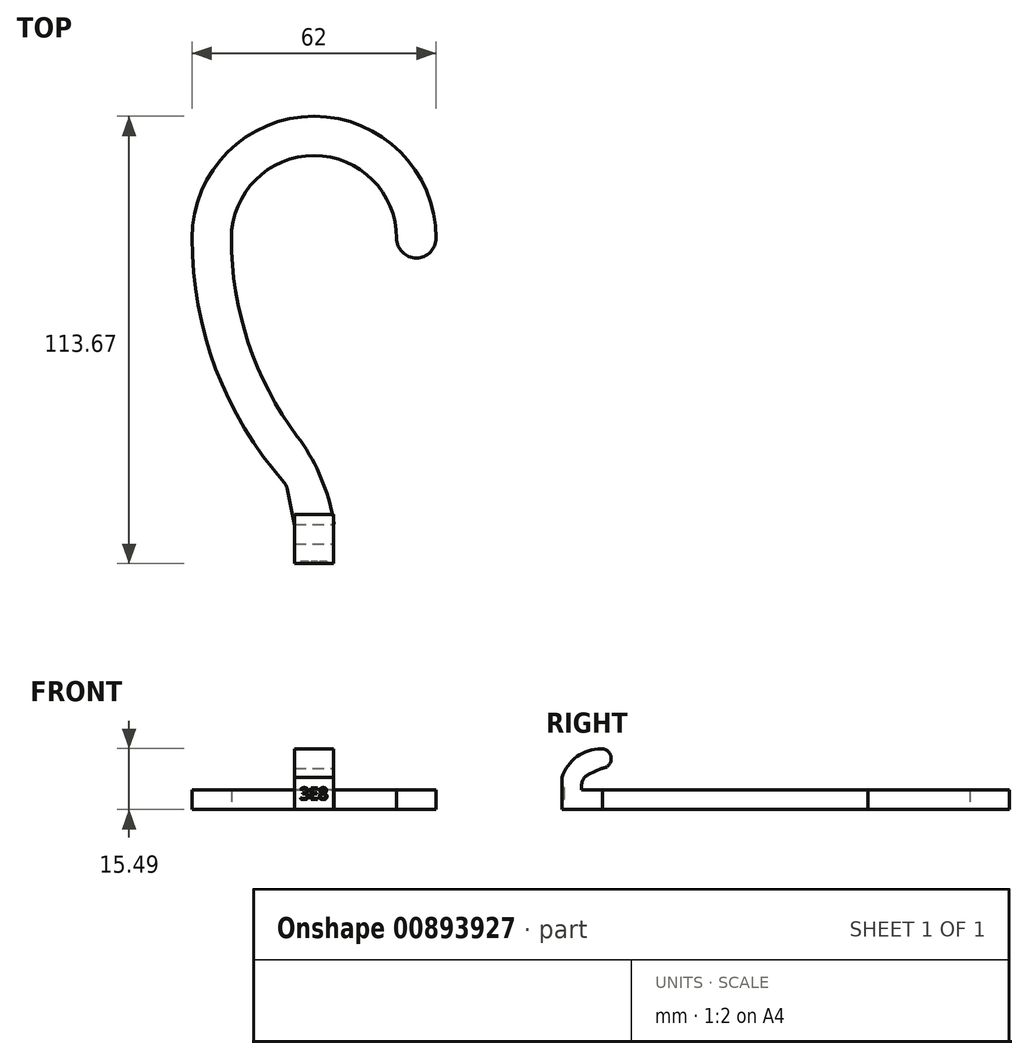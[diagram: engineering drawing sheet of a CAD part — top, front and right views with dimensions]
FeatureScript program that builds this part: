
annotation { "Feature Type Name" : "Feature", "Feature Type Description" : "" }
export const myFeature = defineFeature(function(context is Context, id is Id, definition is map)
    precondition{}
    {
        {
            assignVariable(context, id + "F0", {"name" : "hangerwidth", "anyValue" : 10});
        }
        {
            var Q0;
            Q0=qCreatedBy(makeId("Top.planeOp"),FACE);
            var sketch = newSketch(context, id + "F1", { "sketchPlane" : qUnion([Q0])});
            skArc(sketch, "E0", {"start": v(21, 0) * mm, "mid": v(0, 21) * mm, "end": v(-21, 0) * mm});
            skLineSegment(sketch, "E1", {"start": v(-21, 0) * mm, "end": v(21, 0) * mm, "construction": true});
            skArc(sketch, "E2", {"start": v(21, 0) * mm, "mid": v(26, -5) * mm, "end": v(31, 0) * mm});
            skArc(sketch, "E3", {"start": v(31, 0) * mm, "mid": v(0, 31) * mm, "end": v(-31, 0) * mm});
            skLineSegment(sketch, "E4", {"start": v(21, 0) * mm, "end": v(31, 0) * mm, "construction": true});
            skArc(sketch, "E5", {"start": v(-31, 0) * mm, "mid": v(-24.81, -33.54) * mm, "end": v(-7.06, -62.67) * mm});
            skArc(sketch, "E6", {"start": v(-21, 0) * mm, "mid": v(-13.66, -34.33) * mm, "end": v(7.06, -62.67) * mm});
            skLineSegment(sketch, "E7", {"start": v(-7.06, -62.67) * mm, "end": v(-5, -72.67) * mm});
            skLineSegment(sketch, "E8", {"start": v(-5, -72.67) * mm, "end": v(-5, -82.67) * mm});
            skLineSegment(sketch, "E9", {"start": v(-5, -82.67) * mm, "end": v(5, -82.67) * mm});
            skLineSegment(sketch, "E10", {"start": v(5, -82.67) * mm, "end": v(5, -72.67) * mm});
            skLineSegment(sketch, "E11", {"start": v(5, -72.67) * mm, "end": v(7.06, -62.67) * mm});
            skLineSegment(sketch, "E12", {"start": v(-7.06, -62.67) * mm, "end": v(7.06, -62.67) * mm, "construction": true});
            skLineSegment(sketch, "E13", {"start": v(0, -62.67) * mm, "end": v(0, -82.67) * mm, "construction": true});
            skSolve(sketch);
        }
        {
            var Q0;
            Q0 = qSketchRegion(id + "F1", true);
            extrude(context, id + "F2", {"entities" : qUnion([Q0]), "depth" : (getVariable(context, 'hangerwidth') / 2) * mm, "offsetDistance" : 25 * mm});
        }
        {
            var Q0;
            Q0=makeQuery(id+"F2.opExtrude","SWEPT_FACE",FACE,{"disambiguationData":[OSD([sQuery(id+"F1.wireOp",EDGE,"E10")])]});
            var sketch = newSketch(context, id + "F3", { "sketchPlane" : qUnion([Q0])});
            skLineSegment(sketch, "E14.0", {"start": v(-82.67, 5) * mm, "end": v(-72.67, 5) * mm});
            skLineSegment(sketch, "E15", {"start": v(-82.67, 5) * mm, "end": v(-82.67, 8.15) * mm});
            skArc(sketch, "E16", {"start": v(-72.67, 15.49) * mm, "mid": v(-78.87, 13.46) * mm, "end": v(-82.67, 8.15) * mm});
            skArc(sketch, "E17", {"start": v(-72.67, 10.49) * mm, "mid": v(-70.17, 12.99) * mm, "end": v(-72.67, 15.49) * mm});
            skLineSegment(sketch, "E18", {"start": v(-77.67, 8.15) * mm, "end": v(-77.67, 5) * mm});
            skLineSegment(sketch, "E19", {"start": v(-72.67, 15.49) * mm, "end": v(-72.67, 10.49) * mm, "construction": true});
            skLineSegment(sketch, "E20", {"start": v(-72.67, 10.49) * mm, "end": v(-77.67, 8.15) * mm});
            skSolve(sketch);
        }
        {
            var Q0;
            Q0 = qSketchRegion(id + "F3", true);
            var Q1;
            Q1=makeQuery(id+"F2.opExtrude","SWEPT_FACE",FACE,{"disambiguationData":[OSD([sQuery(id+"F1.wireOp",EDGE,"E8")])]});
            extrude(context, id + "F4", {"entities" : qUnion([Q0]), "operationType" : NewBodyOperationType.ADD, "endBound" : BoundingType.UP_TO_SURFACE, "oppositeDirection" : true, "depth" : 25 * mm, "endBoundEntityFace" : qUnion([Q1]), "offsetDistance" : 25 * mm});
        }
        {
            var Q0;
            Q0=makeQuery(id+"F4.boolean.opBoolean","MERGE",FACE,{"derivedFrom":[makeQuery(id+"F2.opExtrude","SWEPT_FACE",FACE,{"disambiguationData":[OSD([sQuery(id+"F1.wireOp",EDGE,"E9")])]}),makeQuery(id+"F4.opExtrude","SWEPT_FACE",FACE,{"disambiguationData":[OSD([sQuery(id+"F3.wireOp",EDGE,"E15")])]})]});
            var sketch = newSketch(context, id + "F5", { "sketchPlane" : qUnion([Q0])});
            skLineSegment(sketch, "E21", {"start": v(-5, 8.15) * mm, "end": v(5, 0) * mm, "construction": true});
            skText(sketch, "E22", { "text": "3E8", "fontName": "OpenSans-Regular.ttf"});
            skPoint(sketch, "E23", {"position": v(0, 4.08) * mm});
            const initialGuessF5  = {"E22": [-0.00357, 0.00258, 1, 0, 0.003]};
            skSetInitialGuess(sketch, initialGuessF5);
            skSolve(sketch);
        }
        {
            var Q0;
            Q0 = qSketchRegion(id + "F5", true);
            extrude(context, id + "F6", {"entities" : qUnion([Q0]), "operationType" : NewBodyOperationType.REMOVE, "oppositeDirection" : true, "depth" : .5 * mm, "offsetDistance" : 25 * mm});
        }
        {
            var Q0;
            Q0=makeQuery(id+"F2.opExtrude","SWEPT_EDGE",EDGE,{"disambiguationData":[OSD([sQuery(id+"F1.wireOp",EDGE,"E5"),sQuery(id+"F1.wireOp",EDGE,"E7")])]});
            var Q1;
            Q1=makeQuery(id+"F2.opExtrude","SWEPT_EDGE",EDGE,{"disambiguationData":[OSD([sQuery(id+"F1.wireOp",EDGE,"E7"),sQuery(id+"F1.wireOp",EDGE,"E8")])]});
            var Q2;
            Q2=makeQuery(id+"F2.opExtrude","SWEPT_EDGE",EDGE,{"disambiguationData":[OSD([sQuery(id+"F1.wireOp",EDGE,"E10"),sQuery(id+"F1.wireOp",EDGE,"E11")])]});
            var Q3;
            Q3=makeQuery(id+"F4.opExtrude","SWEPT_EDGE",EDGE,{"disambiguationData":[OSD([sQuery(id+"F3.wireOp",EDGE,"E14.0"),sQuery(id+"F3.wireOp",EDGE,"E18")])]});
            var Q4;
            Q4=makeQuery(id+"F4.opExtrude","SWEPT_EDGE",EDGE,{"disambiguationData":[OSD([sQuery(id+"F3.wireOp",EDGE,"E18"),sQuery(id+"F3.wireOp",EDGE,"E20")])]});
            fillet(context, id + "F7", {"entities" : qUnion([Q0, Q1, Q2, Q3, Q4]), "radius" : (getVariable(context, 'hangerwidth') * .3) * mm, "tangentPropagation" : true, "allowEdgeOverflow" : false});
        }
        {
            var Q0;
            Q0=makeQuery(id+"F2.opExtrude","SWEPT_EDGE",EDGE,{"disambiguationData":[OSD([sQuery(id+"F1.wireOp",EDGE,"E6"),sQuery(id+"F1.wireOp",EDGE,"E11")])]});
            fillet(context, id + "F8", {"entities" : qUnion([Q0]), "radius" : 50 * mm, "tangentPropagation" : true, "allowEdgeOverflow" : false});
        }
    });
